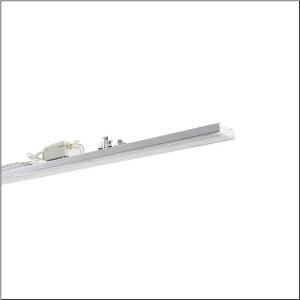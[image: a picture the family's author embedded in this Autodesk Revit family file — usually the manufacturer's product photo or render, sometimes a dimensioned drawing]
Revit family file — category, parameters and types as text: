
# Revit family: licross_21_recessed_mo_52tl18vn48xg
name_source: partatom
category: Lighting Fixtures
units: mm (PartAtom-declared; Revit-internal decimal feet)

## family parameters
Cut with Voids When Loaded = No
Host = Face
Light Source = No
Part Type = Normal
Room Calculation Point = No
Round Connector Dimension = Use Diameter
Shared = No

## types (1)
- --- (1 x LED, 8000 lm, 45.7 W, 4000K)
    Apparent Load = 46 VA
    CIE Flux Codes = 79 95 99 100 100
    Color Rendering = 80
    Color Temperature = 4000K
    Default Elevation = 1800 mm
    Description = Licross 21 Recessed MO, luminaire insert, of sheet steel, galvanised, coil coated, white, length: 1.500mm, width: 66mm, height: 67mm, LED rated luminous flux: 8.000lm, light colour: 840, SDCM (Standard Deviation of Colour Matching)MacAdam ≤ 3 SDCM (initial), control gear: DALI 2, CLO, with plug, 5-pole, with phase selection, mains connection: 220..240V, AC, 50/60Hz, start of lifetime: 46W, end of service life: 54W, internal wiring halogen-free, primary optical cover: cover, of PMMA, light emission: direct distribution, primary light characteristic: symmetric, protection rating (complete): IP40, insulation class (complete): insulation class I (protective earthing), certification: CE, ENEC, VDE, UKCA, protection symbol: D if used in an environment without relevant dust loads with corresponding accessories, impact resistance: IK06, permissible ambient temperature for indoor applications: -25..+40°C, corresponds to IFS (International Featured Standards) requirements for safety and quality in the food industry, reducing of maximum allowable ambient temperature of 5°C with ceiling mounting, LABS conformity tested according to VDMA 24364:2018-05, The light source and the operating device comply with the requirements of the Ecodesign Regulation (EU) 2019/2020 and are replaceable in accordance with this regulation, packaging unit: 1 piece
    Height = 58 mm
    Lamp = 1 x LED
    Lamp Light Flux = 8000 lm
    Lamp Power = 45.7 W
    Lamp count = 1
    Length = 1500 mm
    Luminous efficacy = 175 lm/W
    Manufacturer = Siteco
    ModVariant = No
    Model = 52TL18VN48XG
    Mounting Place = Ceiling
    Mounting Type = Pendant
    Number of Poles = 1
    OnlyDefault = Yes
    Power Factor = 1
    Product Name = Licross 21 Recessed MO
    Product group = luminaire insert | ceiling pendant
    ProductGroupID = 901
    Protection Class = Protection class I
    Protection Degree = IP 40
    RLX_Detail_Level = 1
    RLX_Emergency_Light_Flux = 0 lm
    RLX_Emergency_Type = 0
    RLX_Emergency_Type_DB = No
    RlxData = <blob elided: 24833 chars, md5=90adb6ea>
    Socket = socket
    Standby Power = 0 W
    System Light Flux = 8000 lm
    System Power = 46 W
    Type Comments = factory setting: luminous flux: 100 % | dim-lin: 254 | 307 mA
    Type Image = l_1296930.jpg
    URL = http://relux.com
    VarID = @adj_088879
    Voltage = 0 V
    Weight = 0.00 kg
    Width = 66 mm

## geometry (parser evidence)
native form markers: Blend x4, Sweep x13
no freeform markers — native parametric forms only
